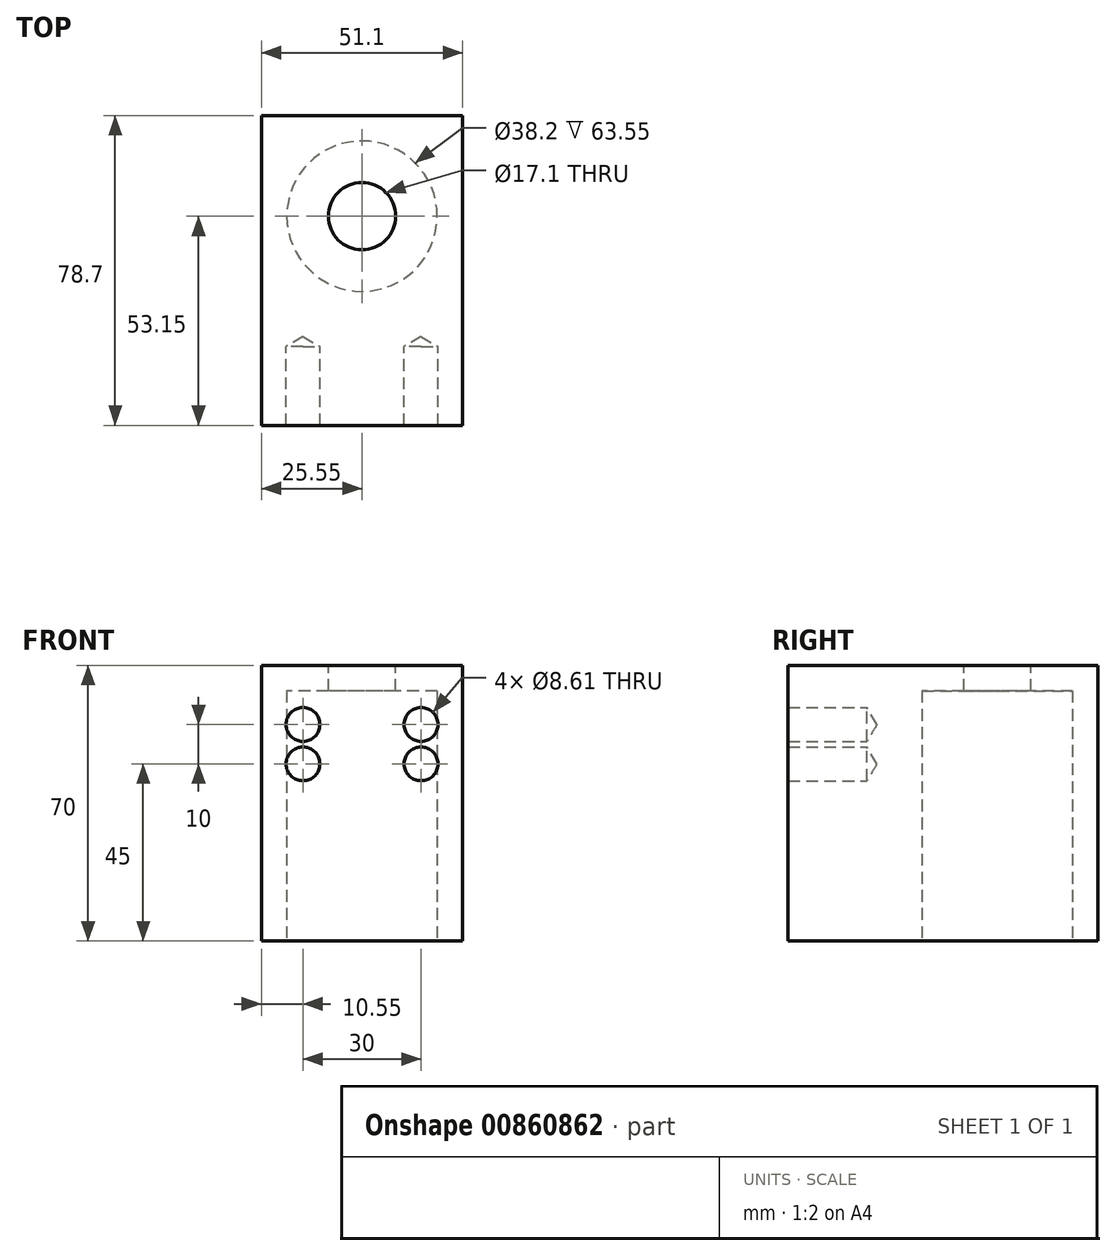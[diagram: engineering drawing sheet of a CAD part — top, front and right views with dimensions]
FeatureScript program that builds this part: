
annotation { "Feature Type Name" : "Feature", "Feature Type Description" : "" }
export const myFeature = defineFeature(function(context is Context, id is Id, definition is map)
    precondition{}
    {
        {
            var Q0;
            Q0=qCreatedBy(makeId("Top.planeOp"),FACE);
            var sketch = newSketch(context, id + "F0", { "sketchPlane" : qUnion([Q0])});
            skLineSegment(sketch, "E0.bottom", {"start": v(25.55, -39.35) * mm, "end": v(-25.55, -39.35) * mm});
            skLineSegment(sketch, "E0.top", {"start": v(25.55, 39.35) * mm, "end": v(-25.55, 39.35) * mm});
            skLineSegment(sketch, "E0.left", {"start": v(25.55, -39.35) * mm, "end": v(25.55, 39.35) * mm});
            skLineSegment(sketch, "E0.right", {"start": v(-25.55, -39.35) * mm, "end": v(-25.55, 39.35) * mm});
            skPoint(sketch, "E0.middle", {"position": v(0, 0) * mm});
            skLineSegment(sketch, "E1", {"start": v(0, 39.35) * mm, "end": v(0, -39.35) * mm});
            skLineSegment(sketch, "E2", {"start": v(25.55, 13.8) * mm, "end": v(-25.55, 13.8) * mm});
            skCircle(sketch, "E3", {"center": v(0, 13.8) * mm, "radius": 19.1 * mm});
            skSolve(sketch);
        }
        {
            var Q0;
            Q0=makeQuery(id+"F0.imprint","IMPRINT",FACE,{"disambiguationData":[TD([[makeQuery(id+"F0.imprint","IMPRINT",EDGE,{"derivedFrom":sQuery(id+"F0.wireOp",EDGE,"E0.bottom")}),-1.0]])]});
            var Q1;
            {var subQ1=sQuery(id+"F0.wireOp",EDGE,"E0.top");var subQ5=sQuery(id+"F0.wireOp",EDGE,"E0.left");var subQ6=makeQuery(id+"F0.imprint","INTERSECT",VERTEX,{"derivedFrom":[subQ1,subQ5]});Q1=makeQuery(id+"F0.imprint","IMPRINT",FACE,{"disambiguationData":[TD([[makeQuery(id+"F0.imprint","IMPRINT",EDGE,{"disambiguationData":[TD([[subQ6,-1.0]])],"derivedFrom":subQ1}),1.0]])]});}
            var Q2;
            {var subQ1=sQuery(id+"F0.wireOp",EDGE,"E0.right");var subQ5=sQuery(id+"F0.wireOp",EDGE,"E0.top");var subQ6=makeQuery(id+"F0.imprint","INTERSECT",VERTEX,{"derivedFrom":[subQ5,subQ1]});Q2=makeQuery(id+"F0.imprint","IMPRINT",FACE,{"disambiguationData":[TD([[makeQuery(id+"F0.imprint","IMPRINT",EDGE,{"disambiguationData":[TD([[subQ6,1.0]])],"derivedFrom":subQ5}),1.0]])]});}
            var Q3;
            {var subQ0=sQuery(id+"F0.wireOp",EDGE,"E3");var subQ1=sQuery(id+"F0.wireOp",EDGE,"E1");var subQ2=makeQuery(id+"F0.imprint","INTERSECT",VERTEX,{"disambiguationData":[OD(0.0)],"derivedFrom":[subQ1,subQ0]});Q3=makeQuery(id+"F0.imprint","IMPRINT",FACE,{"disambiguationData":[TD([[makeQuery(id+"F0.imprint","IMPRINT",EDGE,{"disambiguationData":[TD([[subQ2,-1.0]])],"derivedFrom":subQ1}),1.0]])]});}
            var Q4;
            {var subQ0=sQuery(id+"F0.wireOp",EDGE,"E2");var subQ1=sQuery(id+"F0.wireOp",EDGE,"E1");var subQ2=makeQuery(id+"F0.imprint","INTERSECT",VERTEX,{"derivedFrom":[subQ1,subQ0]});Q4=makeQuery(id+"F0.imprint","IMPRINT",FACE,{"disambiguationData":[TD([[makeQuery(id+"F0.imprint","IMPRINT",EDGE,{"disambiguationData":[TD([[subQ2,-1.0]])],"derivedFrom":subQ1}),1.0]])]});}
            var Q5;
            {var subQ0=sQuery(id+"F0.wireOp",EDGE,"E2");var subQ1=sQuery(id+"F0.wireOp",EDGE,"E1");var subQ2=makeQuery(id+"F0.imprint","INTERSECT",VERTEX,{"derivedFrom":[subQ1,subQ0]});Q5=makeQuery(id+"F0.imprint","IMPRINT",FACE,{"disambiguationData":[TD([[makeQuery(id+"F0.imprint","IMPRINT",EDGE,{"disambiguationData":[TD([[subQ2,-1.0]])],"derivedFrom":subQ1}),-1.0]])]});}
            var Q6;
            {var subQ0=sQuery(id+"F0.wireOp",EDGE,"E3");var subQ1=sQuery(id+"F0.wireOp",EDGE,"E1");var subQ2=makeQuery(id+"F0.imprint","INTERSECT",VERTEX,{"disambiguationData":[OD(0.0)],"derivedFrom":[subQ1,subQ0]});Q6=makeQuery(id+"F0.imprint","IMPRINT",FACE,{"disambiguationData":[TD([[makeQuery(id+"F0.imprint","IMPRINT",EDGE,{"disambiguationData":[TD([[subQ2,-1.0]])],"derivedFrom":subQ1}),-1.0]])]});}
            extrude(context, id + "F1", {"entities" : qUnion([Q0, Q1, Q2, Q3, Q4, Q5, Q6]), "depth" : 70 * mm, "offsetDistance" : 25 * mm});
        }
        {
            var Q0;
            Q0=makeQuery(id+"F1.opExtrude","CAP_FACE",FACE,{"disambiguationData":[OSD([sQuery(id+"F0.wireOp",EDGE,"E0.bottom"),sQuery(id+"F0.wireOp",EDGE,"E0.top"),sQuery(id+"F0.wireOp",EDGE,"E0.left"),sQuery(id+"F0.wireOp",EDGE,"E0.right")])],"isStart":false});
            var sketch = newSketch(context, id + "F2", { "sketchPlane" : qUnion([Q0])});
            skLineSegment(sketch, "E4", {"start": v(0, 39.35) * mm, "end": v(0, -39.35) * mm});
            skLineSegment(sketch, "E5", {"start": v(-25.55, 13.8) * mm, "end": v(25.55, 13.8) * mm});
            skCircle(sketch, "E6", {"center": v(0, 13.8) * mm, "radius": 8.55 * mm});
            skSolve(sketch);
        }
        {
            var Q0;
            {var subQ0=sQuery(id+"F0.wireOp",EDGE,"E3");var subQ1=sQuery(id+"F0.wireOp",EDGE,"E1");var subQ2=makeQuery(id+"F0.imprint","INTERSECT",VERTEX,{"disambiguationData":[OD(0.0)],"derivedFrom":[subQ1,subQ0]});Q0=makeQuery(id+"F0.imprint","IMPRINT",FACE,{"disambiguationData":[TD([[makeQuery(id+"F0.imprint","IMPRINT",EDGE,{"disambiguationData":[TD([[subQ2,-1.0]])],"derivedFrom":subQ1}),-1.0]])]});}
            var Q1;
            {var subQ0=sQuery(id+"F0.wireOp",EDGE,"E3");var subQ1=sQuery(id+"F0.wireOp",EDGE,"E1");var subQ2=makeQuery(id+"F0.imprint","INTERSECT",VERTEX,{"disambiguationData":[OD(0.0)],"derivedFrom":[subQ1,subQ0]});Q1=makeQuery(id+"F0.imprint","IMPRINT",FACE,{"disambiguationData":[TD([[makeQuery(id+"F0.imprint","IMPRINT",EDGE,{"disambiguationData":[TD([[subQ2,-1.0]])],"derivedFrom":subQ1}),1.0]])]});}
            var Q2;
            {var subQ0=sQuery(id+"F0.wireOp",EDGE,"E2");var subQ1=sQuery(id+"F0.wireOp",EDGE,"E1");var subQ2=makeQuery(id+"F0.imprint","INTERSECT",VERTEX,{"derivedFrom":[subQ1,subQ0]});Q2=makeQuery(id+"F0.imprint","IMPRINT",FACE,{"disambiguationData":[TD([[makeQuery(id+"F0.imprint","IMPRINT",EDGE,{"disambiguationData":[TD([[subQ2,-1.0]])],"derivedFrom":subQ1}),1.0]])]});}
            var Q3;
            {var subQ0=sQuery(id+"F0.wireOp",EDGE,"E2");var subQ1=sQuery(id+"F0.wireOp",EDGE,"E1");var subQ2=makeQuery(id+"F0.imprint","INTERSECT",VERTEX,{"derivedFrom":[subQ1,subQ0]});Q3=makeQuery(id+"F0.imprint","IMPRINT",FACE,{"disambiguationData":[TD([[makeQuery(id+"F0.imprint","IMPRINT",EDGE,{"disambiguationData":[TD([[subQ2,-1.0]])],"derivedFrom":subQ1}),-1.0]])]});}
            extrude(context, id + "F3", {"entities" : qUnion([Q0, Q1, Q2, Q3]), "operationType" : NewBodyOperationType.REMOVE, "oppositeDirection" : true, "depth" : -63.55 * mm, "offsetDistance" : 25 * mm});
        }
        {
            var Q0;
            {var subQ0=sQuery(id+"F2.wireOp",EDGE,"E5");var subQ1=sQuery(id+"F2.wireOp",EDGE,"E4");var subQ2=makeQuery(id+"F2.imprint","INTERSECT",VERTEX,{"derivedFrom":[subQ1,subQ0]});Q0=makeQuery(id+"F2.imprint","IMPRINT",FACE,{"disambiguationData":[TD([[makeQuery(id+"F2.imprint","IMPRINT",EDGE,{"disambiguationData":[TD([[subQ2,-1.0]])],"derivedFrom":subQ1}),-1.0]])]});}
            var Q1;
            {var subQ0=sQuery(id+"F2.wireOp",EDGE,"E5");var subQ1=sQuery(id+"F2.wireOp",EDGE,"E4");var subQ2=makeQuery(id+"F2.imprint","INTERSECT",VERTEX,{"derivedFrom":[subQ1,subQ0]});Q1=makeQuery(id+"F2.imprint","IMPRINT",FACE,{"disambiguationData":[TD([[makeQuery(id+"F2.imprint","IMPRINT",EDGE,{"disambiguationData":[TD([[subQ2,-1.0]])],"derivedFrom":subQ1}),1.0]])]});}
            var Q2;
            {var subQ0=sQuery(id+"F2.wireOp",EDGE,"E6");var subQ1=sQuery(id+"F2.wireOp",EDGE,"E4");var subQ2=makeQuery(id+"F2.imprint","INTERSECT",VERTEX,{"disambiguationData":[OD(0.0)],"derivedFrom":[subQ1,subQ0]});Q2=makeQuery(id+"F2.imprint","IMPRINT",FACE,{"disambiguationData":[TD([[makeQuery(id+"F2.imprint","IMPRINT",EDGE,{"disambiguationData":[TD([[subQ2,-1.0]])],"derivedFrom":subQ1}),1.0]])]});}
            var Q3;
            {var subQ0=sQuery(id+"F2.wireOp",EDGE,"E6");var subQ1=sQuery(id+"F2.wireOp",EDGE,"E4");var subQ2=makeQuery(id+"F2.imprint","INTERSECT",VERTEX,{"disambiguationData":[OD(0.0)],"derivedFrom":[subQ1,subQ0]});Q3=makeQuery(id+"F2.imprint","IMPRINT",FACE,{"disambiguationData":[TD([[makeQuery(id+"F2.imprint","IMPRINT",EDGE,{"disambiguationData":[TD([[subQ2,-1.0]])],"derivedFrom":subQ1}),-1.0]])]});}
            extrude(context, id + "F4", {"entities" : qUnion([Q0, Q1, Q2, Q3]), "operationType" : NewBodyOperationType.REMOVE, "oppositeDirection" : true, "depth" : 6.45 * mm, "offsetDistance" : 25 * mm});
        }
        {
            var Q0;
            Q0=makeQuery(id+"F1.opExtrude","SWEPT_FACE",FACE,{"disambiguationData":[OSD([sQuery(id+"F0.wireOp",EDGE,"E0.bottom")])]});
            var sketch = newSketch(context, id + "F5", { "sketchPlane" : qUnion([Q0])});
            skLineSegment(sketch, "E7", {"start": v(-15, 70) * mm, "end": v(-15, 0) * mm});
            skLineSegment(sketch, "E8", {"start": v(15, 70) * mm, "end": v(15, 0) * mm});
            skLineSegment(sketch, "E9", {"start": v(-25.55, 55) * mm, "end": v(25.55, 55) * mm});
            skLineSegment(sketch, "E10", {"start": v(-25.55, 45) * mm, "end": v(25.55, 45) * mm});
            skPoint(sketch, "E11", {"position": v(-15, 55) * mm});
            skPoint(sketch, "E12", {"position": v(15, 55) * mm});
            skPoint(sketch, "E13", {"position": v(15, 45) * mm});
            skPoint(sketch, "E14", {"position": v(-15, 45) * mm});
            skSolve(sketch);
        }
        {
            var Q0;
            Q0=sQuery(id+"F5.wireOp",VERTEX,"E11");
            var Q1;
            Q1=sQuery(id+"F5.wireOp",VERTEX,"E12");
            var Q2;
            Q2=sQuery(id+"F5.wireOp",VERTEX,"E13");
            var Q3;
            Q3=sQuery(id+"F5.wireOp",VERTEX,"E14");
            var Q4;
            Q4=makeQuery(id+"F1.opExtrude","SWEPT_BODY",BODY,{"disambiguationData":[OSD([sQuery(id+"F0.wireOp",EDGE,"E0.bottom"),sQuery(id+"F0.wireOp",EDGE,"E0.top"),sQuery(id+"F0.wireOp",EDGE,"E0.left"),sQuery(id+"F0.wireOp",EDGE,"E0.right")])]});
            hole(context, id + "F6", {"style" : HoleStyle.SIMPLE, "endStyle" : HoleEndStyle.BLIND, "holeDiameter" : 8.6 * mm, "majorDiameter" : 6.35 * mm, "holeDepth" : 20 * mm, "isTappedThrough" : true, "tappedDepth" : 19 * mm, "tapClearance" : 3, "locations" : qUnion([Q0, Q1, Q2, Q3]), "scope" : qUnion([Q4]), "startStyle" : HoleStartStyle.PART});
        }
    });
